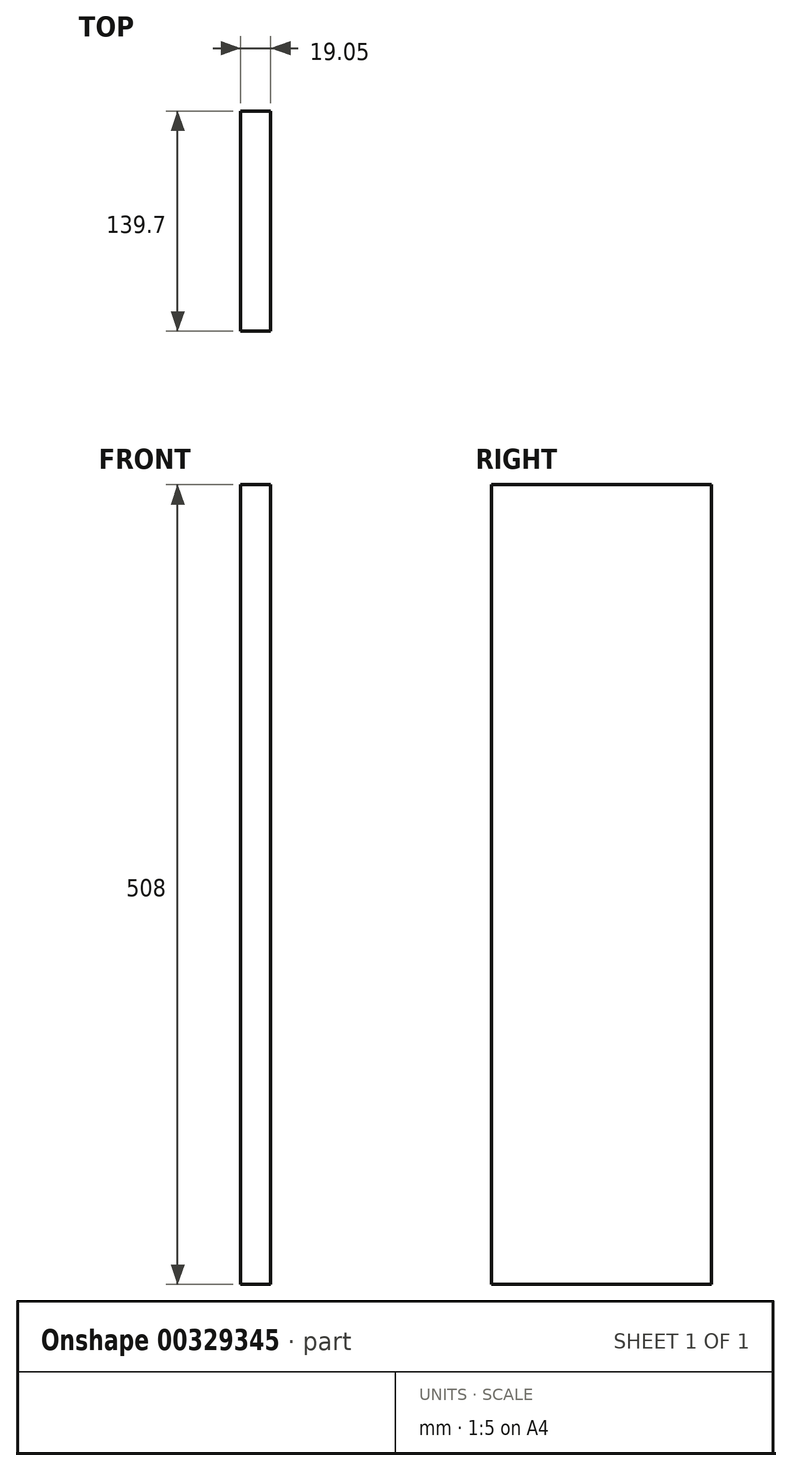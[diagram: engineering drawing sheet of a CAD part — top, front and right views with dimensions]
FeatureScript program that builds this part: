
annotation { "Feature Type Name" : "Feature", "Feature Type Description" : "" }
export const myFeature = defineFeature(function(context is Context, id is Id, definition is map)
    precondition{}
    {
        {
            var Q0;
            Q0=qCreatedBy(makeId("Top.planeOp"),FACE);
            var sketch = newSketch(context, id + "F0", { "sketchPlane" : qUnion([Q0])});
            skLineSegment(sketch, "E0.bottom", {"start": v(0, 0) * mm, "end": v(19.05, 0) * mm});
            skLineSegment(sketch, "E0.top", {"start": v(0, 139.7) * mm, "end": v(19.05, 139.7) * mm});
            skLineSegment(sketch, "E0.left", {"start": v(0, 0) * mm, "end": v(0, 139.7) * mm});
            skLineSegment(sketch, "E0.right", {"start": v(19.05, 0) * mm, "end": v(19.05, 139.7) * mm});
            skSolve(sketch);
        }
        {
            var Q0;
            Q0=makeQuery(id+"F0.imprint","IMPRINT",FACE,{"disambiguationData":[TD([[makeQuery(id+"F0.imprint","IMPRINT",EDGE,{"derivedFrom":sQuery(id+"F0.wireOp",EDGE,"E0.bottom")}),1.0]])]});
            extrude(context, id + "F1", {"entities" : qUnion([Q0]), "depth" : 508 * mm});
        }
    });
